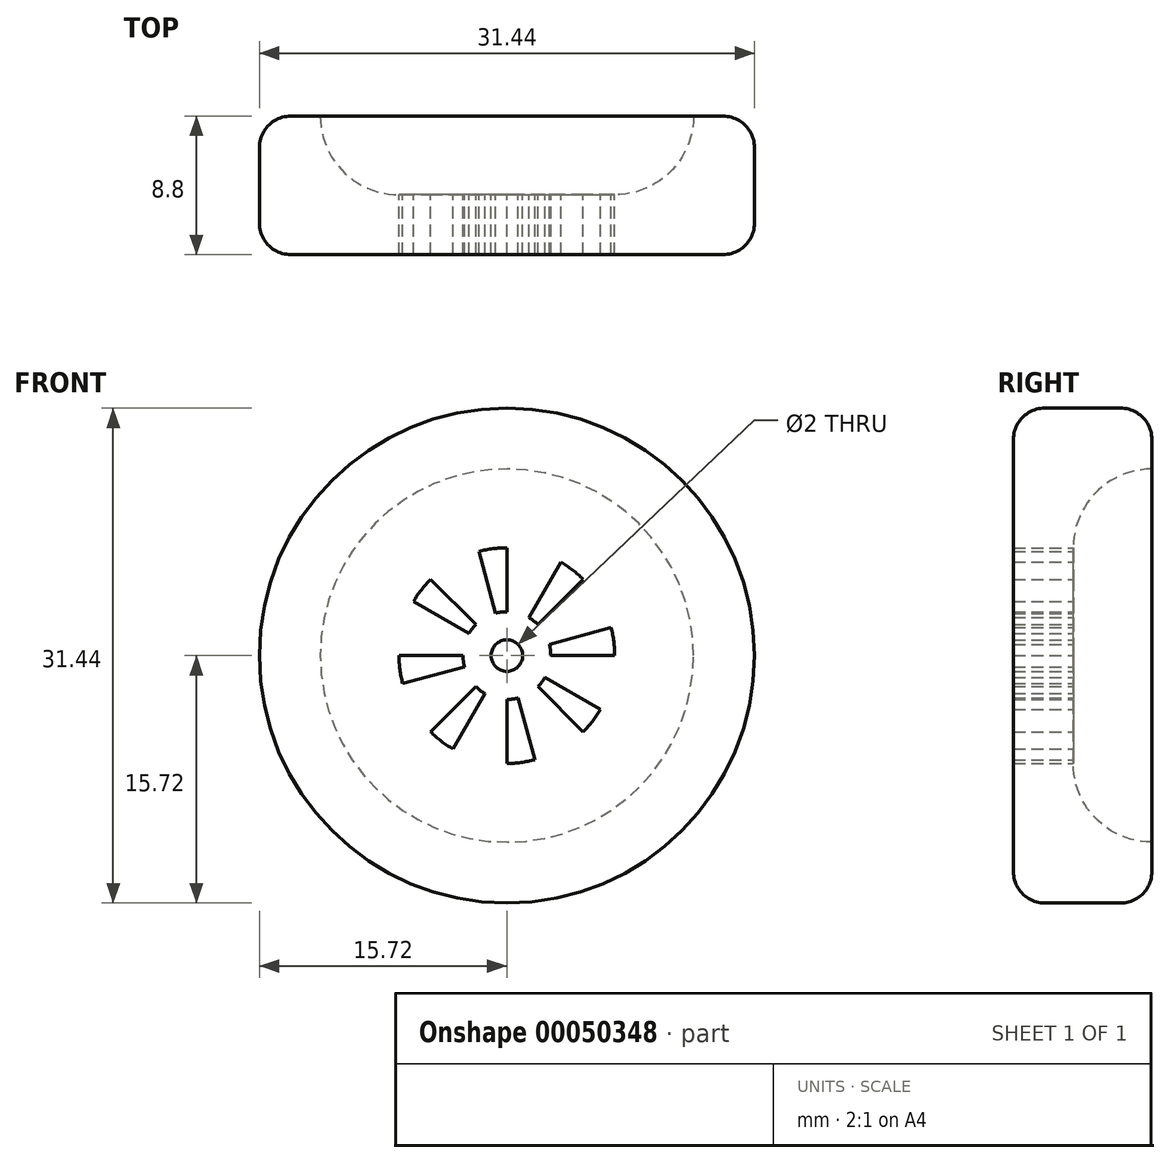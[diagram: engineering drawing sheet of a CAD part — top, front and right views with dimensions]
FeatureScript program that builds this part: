
annotation { "Feature Type Name" : "Feature", "Feature Type Description" : "" }
export const myFeature = defineFeature(function(context is Context, id is Id, definition is map)
    precondition{}
    {
        {
            var Q0;
            Q0=qCreatedBy(makeId("Top.planeOp"),FACE);
            var sketch = newSketch(context, id + "F0", { "sketchPlane" : qUnion([Q0])});
            skLineSegment(sketch, "E0", {"start": v(0, 0) * mm, "end": v(0, 10) * mm});
            skLineSegment(sketch, "E1", {"start": v(0, 0) * mm, "end": v(15.72, 0) * mm});
            skLineSegment(sketch, "E2", {"start": v(15.72, 0) * mm, "end": v(15.72, 8.8) * mm});
            skLineSegment(sketch, "E3", {"start": v(15.72, 8.8) * mm, "end": v(11.85, 8.8) * mm});
            skLineSegment(sketch, "E4", {"start": v(11.85, 8.8) * mm, "end": v(11.85, 8.8) * mm});
            skLineSegment(sketch, "E5", {"start": v(6.85, 3.8) * mm, "end": v(0, 3.8) * mm});
            skPoint(sketch, "E6.visualSharp", {"position": v(11.85, 3.8) * mm});
            skArc(sketch, "E6.filletArc", {"start": v(6.85, 3.8) * mm, "mid": v(10.39, 5.26) * mm, "end": v(11.85, 8.8) * mm});
            skSolve(sketch);
        }
        {
            var Q0;
            {var subQ0=sQuery(id+"F0.wireOp",EDGE,"E1");Q0=makeQuery(id+"F0.imprint","IMPRINT",FACE,{"disambiguationData":[TD([[makeQuery(id+"F0.imprint","IMPRINT",EDGE,{"derivedFrom":subQ0}),1.0]])]});}
            var Q1;
            Q1=sQuery(id+"F0.wireOp",EDGE,"E0");
            revolve(context, id + "F1", {"entities" : qUnion([Q0]), "axis" : qUnion([Q1]), "revolveType" : RevolveType.FULL});
        }
        {
            var Q0;
            Q0=makeQuery(id+"F1.opRevolve","SWEPT_FACE",FACE,{"disambiguationData":[OSD([sQuery(id+"F0.wireOp",EDGE,"E3")])]});
            var sketch = newSketch(context, id + "F2", { "sketchPlane" : qUnion([Q0])});
            skArc(sketch, "E7", {"start": v(0.72, 2.7) * mm, "mid": v(0.36, 2.76) * mm, "end": v(0, 2.79) * mm});
            skArc(sketch, "E8.0", {"start": v(0, 6.85) * mm, "mid": v(0.9, 6.8) * mm, "end": v(1.77, 6.62) * mm});
            skLineSegment(sketch, "E9", {"start": v(0, 2.79) * mm, "end": v(0, 6.85) * mm});
            skLineSegment(sketch, "E10", {"start": v(0.72, 2.7) * mm, "end": v(1.77, 6.62) * mm});
            skArc(sketch, "E11.1.0", {"start": v(-4.84, 4.84) * mm, "mid": v(-4.17, 5.43) * mm, "end": v(-3.42, 5.93) * mm});
            skLineSegment(sketch, "E11.1.1", {"start": v(-1.97, 1.97) * mm, "end": v(-4.84, 4.84) * mm});
            skLineSegment(sketch, "E11.1.2", {"start": v(-1.4, 2.41) * mm, "end": v(-3.42, 5.93) * mm});
            skArc(sketch, "E11.1.3", {"start": v(-1.4, 2.41) * mm, "mid": v(-1.7, 2.21) * mm, "end": v(-1.97, 1.97) * mm});
            skArc(sketch, "E11.2.0", {"start": v(-6.85, 0) * mm, "mid": v(-6.8, 0.9) * mm, "end": v(-6.62, 1.77) * mm});
            skLineSegment(sketch, "E11.2.1", {"start": v(-2.79, 0) * mm, "end": v(-6.85, 0) * mm});
            skLineSegment(sketch, "E11.2.2", {"start": v(-2.7, 0.72) * mm, "end": v(-6.62, 1.77) * mm});
            skArc(sketch, "E11.2.3", {"start": v(-2.7, 0.72) * mm, "mid": v(-2.76, 0.36) * mm, "end": v(-2.79, 0) * mm});
            skArc(sketch, "E11.3.0", {"start": v(-4.84, -4.84) * mm, "mid": v(-5.43, -4.17) * mm, "end": v(-5.93, -3.42) * mm});
            skLineSegment(sketch, "E11.3.1", {"start": v(-1.97, -1.97) * mm, "end": v(-4.84, -4.84) * mm});
            skLineSegment(sketch, "E11.3.2", {"start": v(-2.41, -1.4) * mm, "end": v(-5.93, -3.42) * mm});
            skArc(sketch, "E11.3.3", {"start": v(-2.41, -1.4) * mm, "mid": v(-2.21, -1.7) * mm, "end": v(-1.97, -1.97) * mm});
            skArc(sketch, "E11.4.0", {"start": v(0, -6.85) * mm, "mid": v(-0.9, -6.8) * mm, "end": v(-1.77, -6.62) * mm});
            skLineSegment(sketch, "E11.4.1", {"start": v(0, -2.79) * mm, "end": v(0, -6.85) * mm});
            skLineSegment(sketch, "E11.4.2", {"start": v(-0.72, -2.7) * mm, "end": v(-1.77, -6.62) * mm});
            skArc(sketch, "E11.4.3", {"start": v(-0.72, -2.7) * mm, "mid": v(-0.36, -2.76) * mm, "end": v(0, -2.79) * mm});
            skArc(sketch, "E11.5.0", {"start": v(4.84, -4.84) * mm, "mid": v(4.17, -5.43) * mm, "end": v(3.42, -5.93) * mm});
            skLineSegment(sketch, "E11.5.1", {"start": v(1.97, -1.97) * mm, "end": v(4.84, -4.84) * mm});
            skLineSegment(sketch, "E11.5.2", {"start": v(1.4, -2.41) * mm, "end": v(3.42, -5.93) * mm});
            skArc(sketch, "E11.5.3", {"start": v(1.4, -2.41) * mm, "mid": v(1.7, -2.21) * mm, "end": v(1.97, -1.97) * mm});
            skArc(sketch, "E11.6.0", {"start": v(6.85, 0) * mm, "mid": v(6.8, -0.9) * mm, "end": v(6.62, -1.77) * mm});
            skLineSegment(sketch, "E11.6.1", {"start": v(2.79, 0) * mm, "end": v(6.85, 0) * mm});
            skLineSegment(sketch, "E11.6.2", {"start": v(2.7, -0.72) * mm, "end": v(6.62, -1.77) * mm});
            skArc(sketch, "E11.6.3", {"start": v(2.7, -0.72) * mm, "mid": v(2.76, -0.36) * mm, "end": v(2.79, 0) * mm});
            skArc(sketch, "E11.7.0", {"start": v(4.84, 4.84) * mm, "mid": v(5.43, 4.17) * mm, "end": v(5.93, 3.42) * mm});
            skLineSegment(sketch, "E11.7.1", {"start": v(1.97, 1.97) * mm, "end": v(4.84, 4.84) * mm});
            skLineSegment(sketch, "E11.7.2", {"start": v(2.41, 1.4) * mm, "end": v(5.93, 3.42) * mm});
            skArc(sketch, "E11.7.3", {"start": v(2.41, 1.4) * mm, "mid": v(2.21, 1.7) * mm, "end": v(1.97, 1.97) * mm});
            skCircle(sketch, "E12", {"center": v(0, 0) * mm, "radius": 1 * mm});
            skSolve(sketch);
        }
        {
            var Q0;
            Q0 = qSketchRegion(id + "F2", true);
            var Q1;
            Q1=makeQuery(id+"F1.opRevolve","SWEPT_FACE",FACE,{"disambiguationData":[OSD([sQuery(id+"F0.wireOp",EDGE,"E1")])]});
            extrude(context, id + "F3", {"entities" : qUnion([Q0]), "operationType" : NewBodyOperationType.REMOVE, "endBound" : BoundingType.UP_TO_SURFACE, "oppositeDirection" : true, "endBoundEntityFace" : qUnion([Q1]), "depth" : 25 * mm});
        }
        {
            var Q0;
            Q0=makeQuery(id+"F1.opRevolve","SWEPT_EDGE",EDGE,{"disambiguationData":[OSD([sQuery(id+"F0.wireOp",EDGE,"E2"),sQuery(id+"F0.wireOp",EDGE,"E3")])]});
            fillet(context, id + "F4", {"entities" : qUnion([Q0]), "radius" : 2 * mm, "tangentPropagation" : true, "allowEdgeOverflow" : false});
        }
        {
            var Q0;
            Q0=makeQuery(id+"F1.opRevolve","SWEPT_EDGE",EDGE,{"disambiguationData":[OSD([sQuery(id+"F0.wireOp",EDGE,"E1"),sQuery(id+"F0.wireOp",EDGE,"E2")])]});
            fillet(context, id + "F5", {"entities" : qUnion([Q0]), "radius" : 2 * mm, "tangentPropagation" : true, "allowEdgeOverflow" : false});
        }
    });
